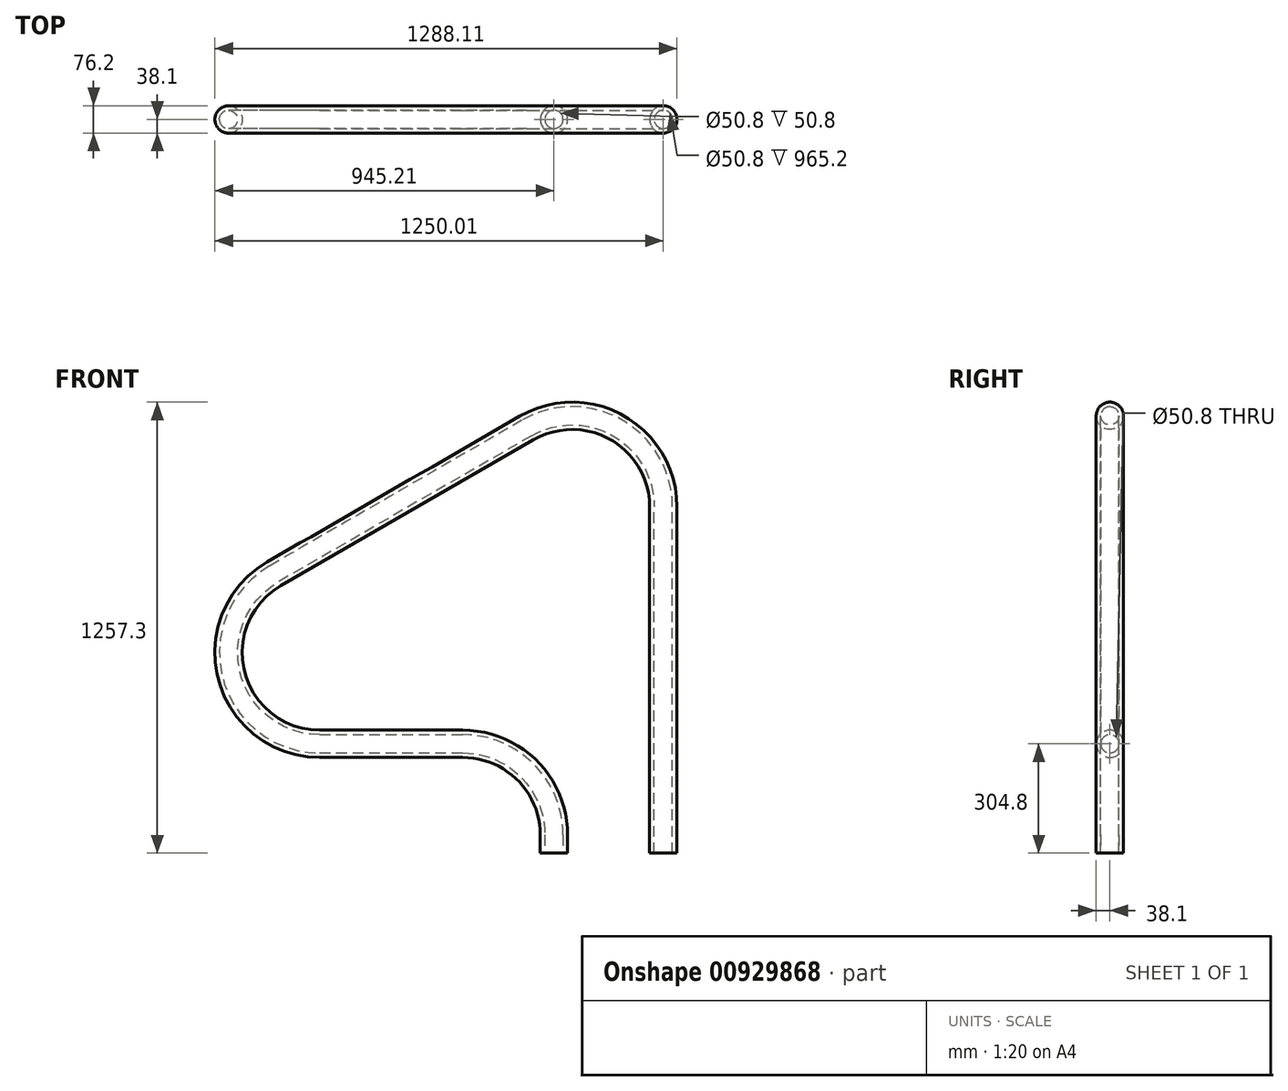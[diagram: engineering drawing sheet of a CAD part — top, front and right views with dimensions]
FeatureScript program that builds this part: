
annotation { "Feature Type Name" : "Feature", "Feature Type Description" : "" }
export const myFeature = defineFeature(function(context is Context, id is Id, definition is map)
    precondition{}
    {
        {
            var Q0;
            Q0=qCreatedBy(makeId("Front.planeOp"),FACE);
            var sketch = newSketch(context, id + "F0", { "sketchPlane" : qUnion([Q0])});
            skLineSegment(sketch, "E0", {"start": v(0, 0) * mm, "end": v(0, 965.2) * mm});
            skLineSegment(sketch, "E1", {"start": v(-381, 1185.17) * mm, "end": v(-1084.9, 778.77) * mm});
            skLineSegment(sketch, "E2", {"start": v(-957.9, 304.8) * mm, "end": v(-558.8, 304.8) * mm});
            skLineSegment(sketch, "E3", {"start": v(-304.8, 50.8) * mm, "end": v(-304.8, 0) * mm});
            skPoint(sketch, "E4.visualSharp", {"position": v(0, 1405.14) * mm});
            skArc(sketch, "E5.filletArc", {"start": v(0, 965.2) * mm, "mid": v(-127, 1185.17) * mm, "end": v(-381, 1185.17) * mm});
            skPoint(sketch, "E6.visualSharp", {"position": v(-1905.85, 304.8) * mm});
            skArc(sketch, "E6.filletArc", {"start": v(-1084.9, 778.77) * mm, "mid": v(-1203.25, 493.06) * mm, "end": v(-957.9, 304.8) * mm});
            skPoint(sketch, "E7.visualSharp", {"position": v(-304.8, 304.8) * mm});
            skArc(sketch, "E7.filletArc", {"start": v(-304.8, 50.8) * mm, "mid": v(-379.2, 230.4) * mm, "end": v(-558.8, 304.8) * mm});
            skLineSegment(sketch, "E8", {"start": v(-299.15, 1219.2) * mm, "end": v(33.74, 1219.2) * mm, "construction": true});
            skSolve(sketch);
        }
        {
            var Q0;
            Q0=sQuery(id+"F0.wireOp",VERTEX,"E0.start");
            var Q1;
            Q1=sQuery(id+"F0.wireOp",EDGE,"E0");
            cPlane(context, id + "F1", {"entities" : qUnion([Q0, Q1]), "cplaneType" : CPlaneType.LINE_POINT, "offset" : 25.4 * mm, "width" : 152.4 * mm, "height" : 152.4 * mm});
        }
        {
            var Q0;
            Q0=qCreatedBy(id+"F1.planeOp",FACE);
            var sketch = newSketch(context, id + "F2", { "sketchPlane" : qUnion([Q0])});
            skCircle(sketch, "E9", {"center": v(0, 0) * mm, "radius": 38.1 * mm});
            skCircle(sketch, "E10", {"center": v(0, 0) * mm, "radius": 25.4 * mm});
            skSolve(sketch);
        }
        {
            var Q0;
            Q0=makeQuery(id+"F2.imprint","IMPRINT",FACE,{"disambiguationData":[TD([[makeQuery(id+"F2.imprint","IMPRINT",EDGE,{"derivedFrom":sQuery(id+"F2.wireOp",EDGE,"E9")}),1.0]])]});
            var Q1;
            Q1 = qConstructionFilter(qBodyType(qCreatedBy(id + "F0" ,EDGE), BodyType.WIRE), ConstructionObject.NO);
            sweep(context, id + "F3", {"profiles" : qUnion([Q0]), "path" : qUnion([Q1])});
        }
    });
